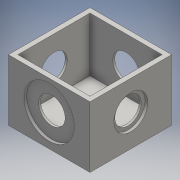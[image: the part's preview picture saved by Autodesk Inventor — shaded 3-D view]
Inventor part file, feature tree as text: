
AUTODESK INVENTOR PART (.ipt)
format: ipt  version: 2016 (Build 200138000, 138)  size: 156,672 bytes
history: native  units: mm
features: extrude x5, sketch x5, mirror x2, pattern_circular x1
ambient origin geometry x8: Origin, YZ Plane, XZ Plane, XY Plane, X Axis, Y Axis, Z Axis, Center Point
bodies: Solid1 (feature_tree)
feature tree (13):
  extrude  "Extrusion1"  Depth=60.0mm
  extrude  "Extrusion2"  Depth=30.0mm
  extrude  "Extrusion3"  Depth=53.0mm
  extrude  "Extrusion4"  Depth=53.0mm
  pattern_circular  "Circular Pattern2"  Count=4  [1 undecoded]
  mirror  "Mirror1"
  extrude  "Extrusion6"  Depth=2.0mm
  mirror  "Mirror2"
  sketch  "Sketch1"  dims[d0=60.0mm d1=60.0mm]
  sketch  "Sketch2"  dims[d2=30.0mm d3=30.0mm]
  sketch  "Sketch3"  dims[d4=5.0mm d5=0.0mm d6=53.0mm]
  sketch  "Sketch4"  dims[d7=53.0mm d8=26.5mm]
  sketch  "Sketch6"  dims[d9=26.5mm d10=40.0mm d11=0.0mm d12=37.0mm d13=23.5mm d14=2.0mm d15=0.0mm d19=19.5mm d20=2.0mm d21=0.0mm d22=40.0mm d23=360.0deg d28=25.0mm d29=2.0mm d30=0.0mm]
note: 1 required parameter value undecoded (feature->parameter linkage not recoverable at this tier; creation-order binding heuristic only, values carry confidence <= 0.55)
